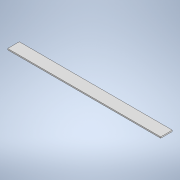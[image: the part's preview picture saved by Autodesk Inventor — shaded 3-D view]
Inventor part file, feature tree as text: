
AUTODESK INVENTOR PART (.ipt)
format: ipt  version: 2020.1 (Build 241239000, 239)  size: 93,696 bytes
history: native  units: mm
features: other x1, extrude x1, sketch x1
ambient origin geometry x8: Origin, YZ Plane, XZ Plane, XY Plane, X Axis, Y Axis, Z Axis, Center Point
bodies: Body1 (feature_tree)
feature tree (3):
  other  "Твердое тело1"
  extrude  "Выдавливание1"  Depth=1000.0mm
  sketch  "Эскиз1"
